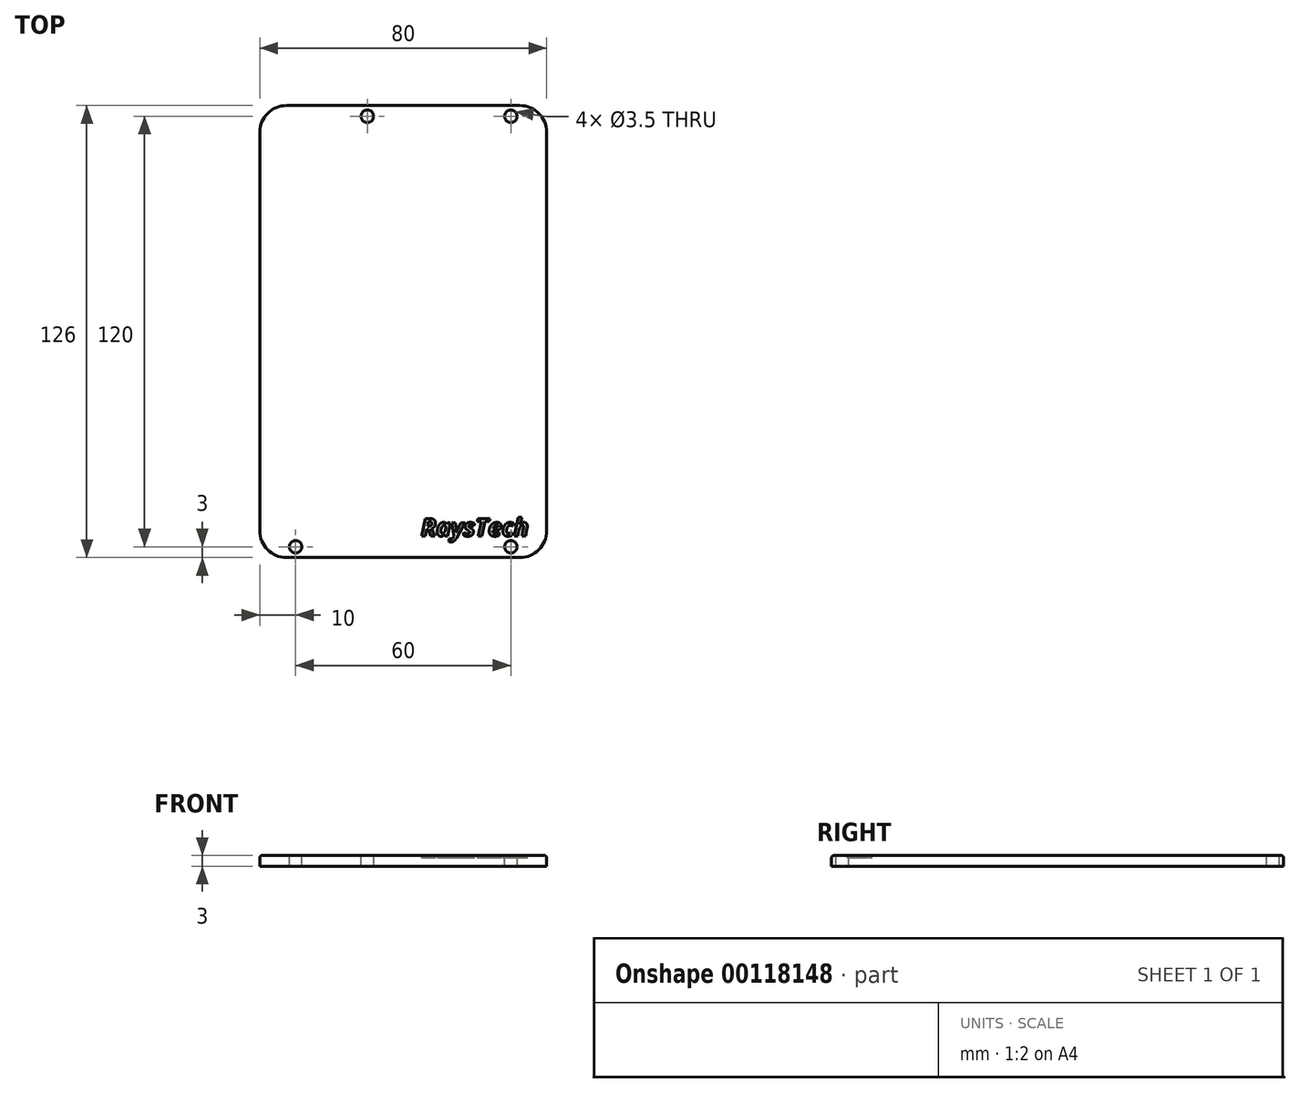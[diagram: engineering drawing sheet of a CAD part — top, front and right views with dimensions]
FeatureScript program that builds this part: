
annotation { "Feature Type Name" : "Feature", "Feature Type Description" : "" }
export const myFeature = defineFeature(function(context is Context, id is Id, definition is map)
    precondition{}
    {
        {
            var Q0;
            Q0=qCreatedBy(makeId("Top.planeOp"),FACE);
            var sketch = newSketch(context, id + "F0", { "sketchPlane" : qUnion([Q0])});
            skLineSegment(sketch, "E0.bottom", {"start": v(-40, 126) * mm, "end": v(40, 126) * mm});
            skLineSegment(sketch, "E0.top", {"start": v(-40, 0) * mm, "end": v(40, 0) * mm});
            skLineSegment(sketch, "E0.left", {"start": v(-40, 126) * mm, "end": v(-40, 0) * mm});
            skLineSegment(sketch, "E0.right", {"start": v(40, 126) * mm, "end": v(40, 0) * mm});
            skSolve(sketch);
        }
        {
            var Q0;
            Q0=makeQuery(id+"F0.imprint","IMPRINT",FACE,{"disambiguationData":[TD([[makeQuery(id+"F0.imprint","IMPRINT",EDGE,{"derivedFrom":sQuery(id+"F0.wireOp",EDGE,"E0.bottom")}),-1.0]])]});
            extrude(context, id + "F1", {"entities" : qUnion([Q0]), "depth" : 3 * mm});
        }
        {
            var Q0;
            {var subQ0=sQuery(id+"F0.wireOp",EDGE,"E0.left");var subQ1=sQuery(id+"F0.wireOp",EDGE,"E0.bottom");var subQ2=sQuery(id+"F0.wireOp",EDGE,"E0.right");var subQ3=sQuery(id+"F0.wireOp",EDGE,"E0.top");Q0=makeQuery(id+"F5.boolean.opBoolean","SPLIT",FACE,{"disambiguationData":[TD([makeQuery(id+"F1.opExtrude","SWEPT_FACE",FACE,{"disambiguationData":[OSD([subQ1])]})])],"derivedFrom":makeQuery(id+"F1.opExtrude","CAP_FACE",FACE,{"disambiguationData":[OSD([subQ1,subQ3,subQ0,subQ2])],"isStart":false})});}
            var sketch = newSketch(context, id + "F2", { "sketchPlane" : qUnion([Q0])});
            skCircle(sketch, "E1", {"center": v(-10, 123) * mm, "radius": 1.75 * mm});
            skCircle(sketch, "E2.1.0.0", {"center": v(30, 123) * mm, "radius": 1.75 * mm});
            skLineSegment(sketch, "E2.direction1", {"start": v(0, 123) * mm, "end": v(40, 123) * mm, "construction": true});
            skCircle(sketch, "E3", {"center": v(-30, 3) * mm, "radius": 1.75 * mm});
            skCircle(sketch, "E4.1.0.0", {"center": v(30, 3) * mm, "radius": 1.75 * mm});
            skLineSegment(sketch, "E4.direction1", {"start": v(-30, 3) * mm, "end": v(30, 3) * mm, "construction": true});
            skSolve(sketch);
        }
        {
            var Q0;
            Q0=makeQuery(id+"F1.opExtrude","SWEPT_EDGE",EDGE,{"disambiguationData":[OSD([sQuery(id+"F0.wireOp",EDGE,"E0.bottom"),sQuery(id+"F0.wireOp",EDGE,"E0.left")])]});
            var Q1;
            Q1=makeQuery(id+"F1.opExtrude","SWEPT_EDGE",EDGE,{"disambiguationData":[OSD([sQuery(id+"F0.wireOp",EDGE,"E0.top"),sQuery(id+"F0.wireOp",EDGE,"E0.left")])]});
            var Q2;
            Q2=makeQuery(id+"F1.opExtrude","SWEPT_EDGE",EDGE,{"disambiguationData":[OSD([sQuery(id+"F0.wireOp",EDGE,"E0.top"),sQuery(id+"F0.wireOp",EDGE,"E0.right")])]});
            var Q3;
            Q3=makeQuery(id+"F1.opExtrude","SWEPT_EDGE",EDGE,{"disambiguationData":[OSD([sQuery(id+"F0.wireOp",EDGE,"E0.bottom"),sQuery(id+"F0.wireOp",EDGE,"E0.right")])]});
            fillet(context, id + "F3", {"entities" : qUnion([Q0, Q1, Q2, Q3]), "radius" : 7.5 * mm, "tangentPropagation" : true, "allowEdgeOverflow" : false});
        }
        {
            var Q0;
            Q0=makeQuery(id+"F1.opExtrude","CAP_FACE",FACE,{"disambiguationData":[OSD([sQuery(id+"F0.wireOp",EDGE,"E0.bottom"),sQuery(id+"F0.wireOp",EDGE,"E0.top"),sQuery(id+"F0.wireOp",EDGE,"E0.left"),sQuery(id+"F0.wireOp",EDGE,"E0.right")])],"isStart":false});
            var sketch = newSketch(context, id + "F4", { "sketchPlane" : qUnion([Q0])});
            skText(sketch, "E5", { "text": "RaysTech", "fontName": "OpenSans-BoldItalic.ttf"});
            const initialGuessF4  = {"E5": [0.005, 0.006, 1, 0, 0.00493]};
            skSetInitialGuess(sketch, initialGuessF4);
            skSolve(sketch);
        }
        {
            var Q0;
            Q0 = qSketchRegion(id + "F4", true);
            extrude(context, id + "F5", {"entities" : qUnion([Q0]), "operationType" : NewBodyOperationType.REMOVE, "oppositeDirection" : true, "depth" : 0.6 * mm});
        }
        {
            var Q0;
            Q0=makeQuery(id+"F1.opExtrude","CAP_EDGE",EDGE,{"disambiguationData":[OSD([sQuery(id+"F0.wireOp",EDGE,"E0.right")])],"isStart":false});
            fillet(context, id + "F6", {"entities" : qUnion([Q0]), "radius" : 0.8 * mm, "tangentPropagation" : true, "allowEdgeOverflow" : false});
        }
        {
            var Q0;
            Q0=makeQuery(id+"F2.imprint","IMPRINT",FACE,{"disambiguationData":[TD([[makeQuery(id+"F2.imprint","IMPRINT",EDGE,{"derivedFrom":sQuery(id+"F2.wireOp",EDGE,"E3")}),1.0]])]});
            var Q1;
            Q1=makeQuery(id+"F2.imprint","IMPRINT",FACE,{"disambiguationData":[TD([[makeQuery(id+"F2.imprint","IMPRINT",EDGE,{"derivedFrom":sQuery(id+"F2.wireOp",EDGE,"E4.1.0.0")}),1.0]])]});
            var Q2;
            Q2=makeQuery(id+"F2.imprint","IMPRINT",FACE,{"disambiguationData":[TD([[makeQuery(id+"F2.imprint","IMPRINT",EDGE,{"derivedFrom":sQuery(id+"F2.wireOp",EDGE,"E1")}),1.0]])]});
            var Q3;
            Q3=makeQuery(id+"F2.imprint","IMPRINT",FACE,{"disambiguationData":[TD([[makeQuery(id+"F2.imprint","IMPRINT",EDGE,{"derivedFrom":sQuery(id+"F2.wireOp",EDGE,"E2.1.0.0")}),1.0]])]});
            extrude(context, id + "F7", {"entities" : qUnion([Q0, Q1, Q2, Q3]), "operationType" : NewBodyOperationType.REMOVE, "oppositeDirection" : true, "depth" : 25 * mm});
        }
    });
